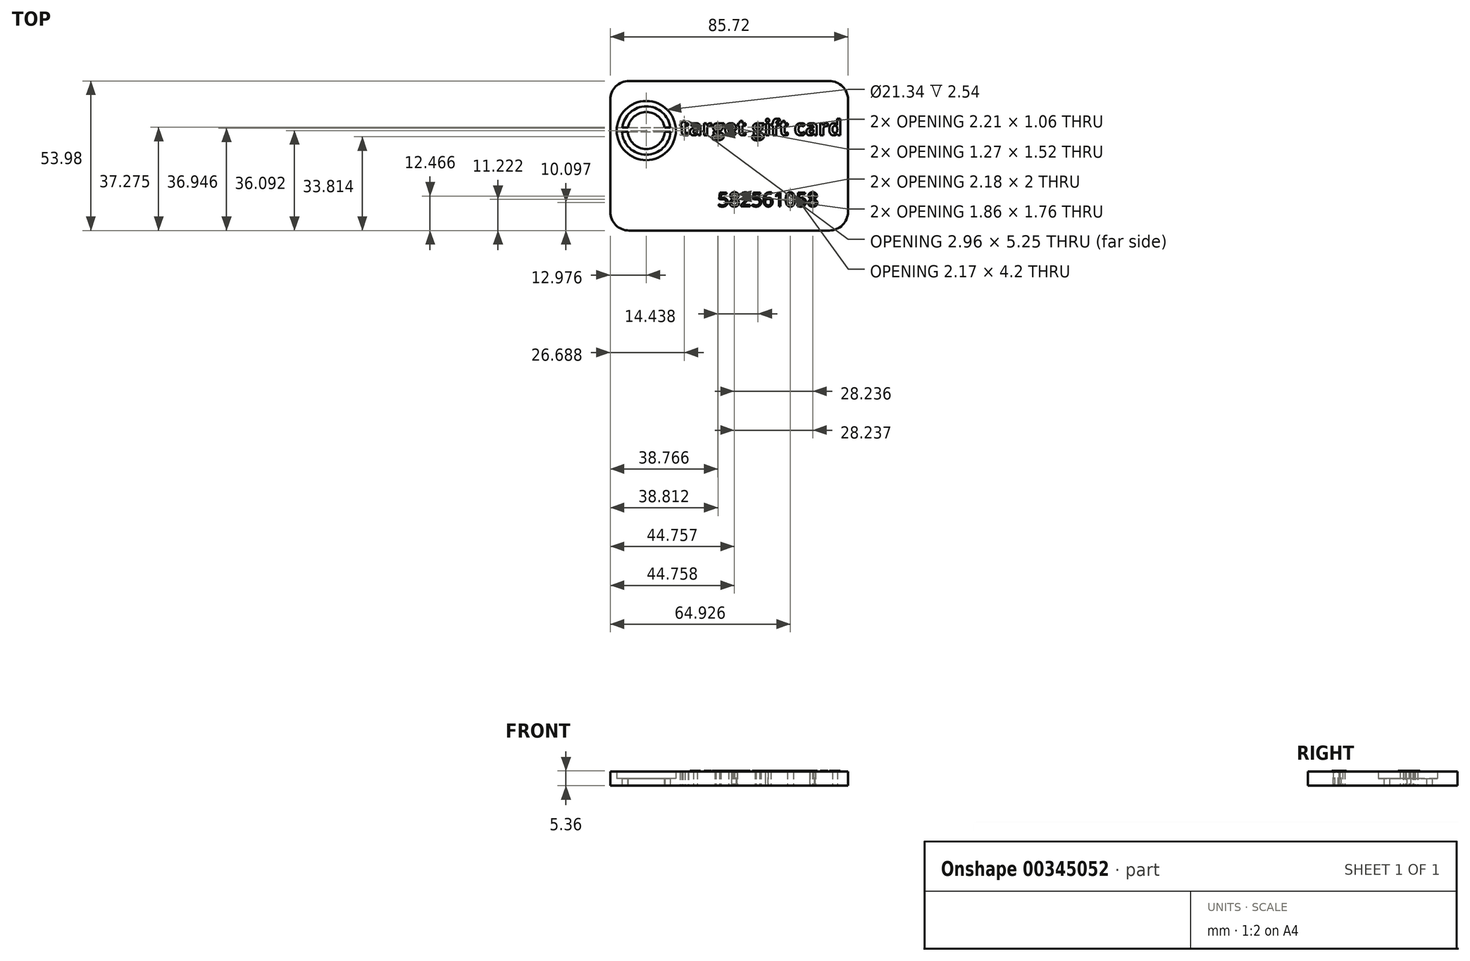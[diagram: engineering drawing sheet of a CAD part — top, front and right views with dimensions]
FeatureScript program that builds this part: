
annotation { "Feature Type Name" : "Feature", "Feature Type Description" : "" }
export const myFeature = defineFeature(function(context is Context, id is Id, definition is map)
    precondition{}
    {
        {
            var Q0;
            Q0=qCreatedBy(makeId("Top.planeOp"),FACE);
            var sketch = newSketch(context, id + "F0", { "sketchPlane" : qUnion([Q0])});
            skLineSegment(sketch, "E0.bottom", {"start": v(-45.51, 28) * mm, "end": v(40.21, 28) * mm});
            skLineSegment(sketch, "E0.top", {"start": v(-45.51, -25.97) * mm, "end": v(40.21, -25.97) * mm});
            skLineSegment(sketch, "E0.left", {"start": v(-45.51, 28) * mm, "end": v(-45.51, -25.97) * mm});
            skLineSegment(sketch, "E0.right", {"start": v(40.21, 28) * mm, "end": v(40.21, -25.97) * mm});
            skCircle(sketch, "E1", {"center": v(-32.53, 10.12) * mm, "radius": 6.68 * mm});
            skCircle(sketch, "E2", {"center": v(-32.53, 10.12) * mm, "radius": 8.74 * mm});
            skCircle(sketch, "E3", {"center": v(-32.53, 10.12) * mm, "radius": 10.67 * mm});
            skText(sketch, "E4", { "text": "target gift card", "fontName": "OpenSans-Bold.ttf"});
            skText(sketch, "E5", { "text": "582561058", "fontName": "OpenSans-Regular.ttf"});
            const initialGuessF0  = {"E4": [-0.02048, 0.00843, 1, 0, 0.00562], "E5": [-0.0068, -0.01727, 1, 0, 0.00508]};
            skSetInitialGuess(sketch, initialGuessF0);
            skSolve(sketch);
        }
        {
            var Q0;
            Q0=makeQuery(id+"F0.imprint","IMPRINT",FACE,{"disambiguationData":[TD([[makeQuery(id+"F0.imprint","IMPRINT",EDGE,{"derivedFrom":sQuery(id+"F0.wireOp",EDGE,"E1")}),1.0]])]});
            var Q1;
            Q1=makeQuery(id+"F0.imprint","IMPRINT",FACE,{"disambiguationData":[TD([[makeQuery(id+"F0.imprint","IMPRINT",EDGE,{"derivedFrom":sQuery(id+"F0.wireOp",EDGE,"E2")}),-1.0]])]});
            extrude(context, id + "F1", {"entities" : qUnion([Q0, Q1]), "depth" : 2.54 * mm});
        }
        {
            var Q0;
            Q0=makeQuery(id+"F0.imprint","IMPRINT",FACE,{"disambiguationData":[TD([[makeQuery(id+"F0.imprint","IMPRINT",EDGE,{"derivedFrom":sQuery(id+"F0.wireOp",EDGE,"E0.bottom")}),-1.0]])]});
            extrude(context, id + "F2", {"entities" : qUnion([Q0]), "operationType" : NewBodyOperationType.ADD, "depth" : 5.08 * mm});
        }
        {
            var Q0;
            Q0=makeQuery(id+"F0.imprint","IMPRINT",FACE,{"disambiguationData":[TD([[makeQuery(id+"F0.imprint","IMPRINT",EDGE,{"derivedFrom":sQuery(id+"F0.wireOp",EDGE,"E0.bottom")}),-1.0]])]});
            var sketch = newSketch(context, id + "F3", { "sketchPlane" : qUnion([Q0])});
            skLineSegment(sketch, "E6.bottom", {"start": v(-43.56, 9.69) * mm, "end": v(-22.85, 9.69) * mm});
            skLineSegment(sketch, "E6.top", {"start": v(-43.56, 11.26) * mm, "end": v(-22.85, 11.26) * mm});
            skLineSegment(sketch, "E6.left", {"start": v(-43.56, 9.69) * mm, "end": v(-43.56, 11.26) * mm});
            skLineSegment(sketch, "E6.right", {"start": v(-22.85, 9.69) * mm, "end": v(-22.85, 11.26) * mm});
            skSolve(sketch);
        }
        {
            var Q0;
            {var subQ0=sQuery(id+"F3.wireOp",EDGE,"E6.right");Q0=makeQuery(id+"F3.imprint","IMPRINT",FACE,{"disambiguationData":[TD([[makeQuery(id+"F3.imprint","IMPRINT",EDGE,{"derivedFrom":subQ0}),1.0]])]});}
            extrude(context, id + "F4", {"entities" : qUnion([Q0]), "operationType" : NewBodyOperationType.ADD, "endBound" : BoundingType.UP_TO_NEXT, "depth" : 25.4 * mm});
        }
        {
            var Q0;
            {var subQ0=sQuery(id+"F3.wireOp",EDGE,"E6.right");Q0=makeQuery(id+"F3.imprint","IMPRINT",FACE,{"disambiguationData":[TD([[makeQuery(id+"F3.imprint","IMPRINT",EDGE,{"derivedFrom":subQ0}),1.0]])]});}
            extrude(context, id + "F5", {"entities" : qUnion([Q0]), "operationType" : NewBodyOperationType.ADD, "depth" : 0 * mm});
        }
        {
            var Q0;
            {var subQ0=sQuery(id+"F3.wireOp",EDGE,"E6.right");Q0=makeQuery(id+"F3.imprint","IMPRINT",FACE,{"disambiguationData":[TD([[makeQuery(id+"F3.imprint","IMPRINT",EDGE,{"derivedFrom":subQ0}),1.0]])]});}
            extrude(context, id + "F6", {"entities" : qUnion([Q0]), "operationType" : NewBodyOperationType.ADD, "oppositeDirection" : true, "depth" : 0.03 * mm});
        }
        {
            var Q0;
            Q0=makeQuery(id+"F0.imprint","IMPRINT",FACE,{"disambiguationData":[TD([[makeQuery(id+"F0.imprint","IMPRINT",EDGE,{"derivedFrom":sQuery(id+"F0.wireOp",EDGE,"E4.sketch_text.stroke-209")}),-1.0]])]});
            var Q1;
            Q1=makeQuery(id+"F0.imprint","IMPRINT",FACE,{"disambiguationData":[TD([[makeQuery(id+"F0.imprint","IMPRINT",EDGE,{"derivedFrom":sQuery(id+"F0.wireOp",EDGE,"E4.sketch_text.stroke-191")}),-1.0]])]});
            var Q2;
            Q2=makeQuery(id+"F0.imprint","IMPRINT",FACE,{"disambiguationData":[TD([[makeQuery(id+"F0.imprint","IMPRINT",EDGE,{"derivedFrom":sQuery(id+"F0.wireOp",EDGE,"E4.sketch_text.stroke-187")}),-1.0]])]});
            var Q3;
            Q3=makeQuery(id+"F0.imprint","IMPRINT",FACE,{"disambiguationData":[TD([[makeQuery(id+"F0.imprint","IMPRINT",EDGE,{"derivedFrom":sQuery(id+"F0.wireOp",EDGE,"E4.sketch_text.stroke-182")}),-1.0]])]});
            var Q4;
            Q4=makeQuery(id+"F0.imprint","IMPRINT",FACE,{"disambiguationData":[TD([[makeQuery(id+"F0.imprint","IMPRINT",EDGE,{"derivedFrom":sQuery(id+"F0.wireOp",EDGE,"E4.sketch_text.stroke-138")}),-1.0]])]});
            var Q5;
            Q5=makeQuery(id+"F0.imprint","IMPRINT",FACE,{"disambiguationData":[TD([[makeQuery(id+"F0.imprint","IMPRINT",EDGE,{"derivedFrom":sQuery(id+"F0.wireOp",EDGE,"E4.sketch_text.stroke-120")}),-1.0]])]});
            var Q6;
            Q6=makeQuery(id+"F0.imprint","IMPRINT",FACE,{"disambiguationData":[TD([[makeQuery(id+"F0.imprint","IMPRINT",EDGE,{"derivedFrom":sQuery(id+"F0.wireOp",EDGE,"E4.sketch_text.stroke-100")}),-1.0]])]});
            var Q7;
            Q7=makeQuery(id+"F0.imprint","IMPRINT",FACE,{"disambiguationData":[TD([[makeQuery(id+"F0.imprint","IMPRINT",EDGE,{"derivedFrom":sQuery(id+"F0.wireOp",EDGE,"E4.sketch_text.stroke-56")}),-1.0]])]});
            var Q8;
            Q8=makeQuery(id+"F0.imprint","IMPRINT",FACE,{"disambiguationData":[TD([[makeQuery(id+"F0.imprint","IMPRINT",EDGE,{"derivedFrom":sQuery(id+"F0.wireOp",EDGE,"E4.sketch_text.stroke-43")}),-1.0]])]});
            var Q9;
            Q9=makeQuery(id+"F0.imprint","IMPRINT",FACE,{"disambiguationData":[TD([[makeQuery(id+"F0.imprint","IMPRINT",EDGE,{"derivedFrom":sQuery(id+"F0.wireOp",EDGE,"E4.sketch_text.stroke-18")}),-1.0]])]});
            var Q10;
            Q10=makeQuery(id+"F0.imprint","IMPRINT",FACE,{"disambiguationData":[TD([[makeQuery(id+"F0.imprint","IMPRINT",EDGE,{"derivedFrom":sQuery(id+"F0.wireOp",EDGE,"E4.sketch_text.stroke-227")}),-1.0]])]});
            var Q11;
            Q11=makeQuery(id+"F0.imprint","IMPRINT",FACE,{"disambiguationData":[TD([[makeQuery(id+"F0.imprint","IMPRINT",EDGE,{"derivedFrom":sQuery(id+"F0.wireOp",EDGE,"E4.sketch_text.stroke-241")}),-1.0]])]});
            var Q12;
            Q12=makeQuery(id+"F0.imprint","IMPRINT",FACE,{"disambiguationData":[TD([[makeQuery(id+"F0.imprint","IMPRINT",EDGE,{"derivedFrom":sQuery(id+"F0.wireOp",EDGE,"E4.sketch_text.stroke-266")}),-1.0]])]});
            var Q13;
            Q13=makeQuery(id+"F0.imprint","IMPRINT",FACE,{"disambiguationData":[TD([[makeQuery(id+"F0.imprint","IMPRINT",EDGE,{"derivedFrom":sQuery(id+"F0.wireOp",EDGE,"E4.sketch_text.stroke-279")}),-1.0]])]});
            var Q14;
            Q14=makeQuery(id+"F0.imprint","IMPRINT",FACE,{"disambiguationData":[TD([[makeQuery(id+"F0.imprint","IMPRINT",EDGE,{"derivedFrom":sQuery(id+"F0.wireOp",EDGE,"E5.sketch_text.stroke-0")}),-1.0]])]});
            var Q15;
            Q15=makeQuery(id+"F0.imprint","IMPRINT",FACE,{"disambiguationData":[TD([[makeQuery(id+"F0.imprint","IMPRINT",EDGE,{"derivedFrom":sQuery(id+"F0.wireOp",EDGE,"E5.sketch_text.stroke-19")}),-1.0]])]});
            var Q16;
            Q16=makeQuery(id+"F0.imprint","IMPRINT",FACE,{"disambiguationData":[TD([[makeQuery(id+"F0.imprint","IMPRINT",EDGE,{"derivedFrom":sQuery(id+"F0.wireOp",EDGE,"E5.sketch_text.stroke-114")}),-1.0]])]});
            var Q17;
            Q17=makeQuery(id+"F0.imprint","IMPRINT",FACE,{"disambiguationData":[TD([[makeQuery(id+"F0.imprint","IMPRINT",EDGE,{"derivedFrom":sQuery(id+"F0.wireOp",EDGE,"E5.sketch_text.stroke-89")}),-1.0]])]});
            var Q18;
            Q18=makeQuery(id+"F0.imprint","IMPRINT",FACE,{"disambiguationData":[TD([[makeQuery(id+"F0.imprint","IMPRINT",EDGE,{"derivedFrom":sQuery(id+"F0.wireOp",EDGE,"E5.sketch_text.stroke-70")}),-1.0]])]});
            var Q19;
            Q19=makeQuery(id+"F0.imprint","IMPRINT",FACE,{"disambiguationData":[TD([[makeQuery(id+"F0.imprint","IMPRINT",EDGE,{"derivedFrom":sQuery(id+"F0.wireOp",EDGE,"E5.sketch_text.stroke-50")}),-1.0]])]});
            var Q20;
            Q20=makeQuery(id+"F0.imprint","IMPRINT",FACE,{"disambiguationData":[TD([[makeQuery(id+"F0.imprint","IMPRINT",EDGE,{"derivedFrom":sQuery(id+"F0.wireOp",EDGE,"E5.sketch_text.stroke-123")}),-1.0]])]});
            var Q21;
            Q21=makeQuery(id+"F0.imprint","IMPRINT",FACE,{"disambiguationData":[TD([[makeQuery(id+"F0.imprint","IMPRINT",EDGE,{"derivedFrom":sQuery(id+"F0.wireOp",EDGE,"E5.sketch_text.stroke-139")}),-1.0]])]});
            var Q22;
            Q22=makeQuery(id+"F0.imprint","IMPRINT",FACE,{"disambiguationData":[TD([[makeQuery(id+"F0.imprint","IMPRINT",EDGE,{"derivedFrom":sQuery(id+"F0.wireOp",EDGE,"E5.sketch_text.stroke-158")}),-1.0]])]});
            extrude(context, id + "F7", {"entities" : qUnion([Q0, Q1, Q2, Q3, Q4, Q5, Q6, Q7, Q8, Q9, Q10, Q11, Q12, Q13, Q14, Q15, Q16, Q17, Q18, Q19, Q20, Q21, Q22]), "operationType" : NewBodyOperationType.ADD, "depth" : 5.33 * mm});
        }
        {
            var Q0;
            Q0=makeQuery(id+"F2.opExtrude","SWEPT_EDGE",EDGE,{"disambiguationData":[OSD([sQuery(id+"F0.wireOp",EDGE,"E0.top"),sQuery(id+"F0.wireOp",EDGE,"E0.right")])]});
            var Q1;
            Q1=makeQuery(id+"F2.opExtrude","SWEPT_EDGE",EDGE,{"disambiguationData":[OSD([sQuery(id+"F0.wireOp",EDGE,"E0.bottom"),sQuery(id+"F0.wireOp",EDGE,"E0.right")])]});
            var Q2;
            Q2=makeQuery(id+"F2.opExtrude","SWEPT_EDGE",EDGE,{"disambiguationData":[OSD([sQuery(id+"F0.wireOp",EDGE,"E0.bottom"),sQuery(id+"F0.wireOp",EDGE,"E0.left")])]});
            var Q3;
            Q3=makeQuery(id+"F2.opExtrude","SWEPT_EDGE",EDGE,{"disambiguationData":[OSD([sQuery(id+"F0.wireOp",EDGE,"E0.top"),sQuery(id+"F0.wireOp",EDGE,"E0.left")])]});
            fillet(context, id + "F8", {"entities" : qUnion([Q0, Q1, Q2, Q3]), "radius" : 6.75 * mm, "tangentPropagation" : true, "allowEdgeOverflow" : false});
        }
        {
            var Q0;
            Q0=makeQuery(id+"F5.boolean.opBoolean","SPLIT",FACE,{"disambiguationData":[OD(1.0)],"derivedFrom":makeQuery(id+"F5.opExtrude","CAP_FACE",FACE,{"disambiguationData":[OSD([sQuery(id+"F0.wireOp",EDGE,"E3"),sQuery(id+"F3.wireOp",EDGE,"E6.bottom"),sQuery(id+"F3.wireOp",EDGE,"E6.top"),sQuery(id+"F3.wireOp",EDGE,"E6.right")])],"isStart":false})});
            var Q1;
            Q1=makeQuery(id+"F5.boolean.opBoolean","SPLIT",FACE,{"disambiguationData":[OD(0.0)],"derivedFrom":makeQuery(id+"F5.opExtrude","CAP_FACE",FACE,{"disambiguationData":[OSD([sQuery(id+"F0.wireOp",EDGE,"E3"),sQuery(id+"F3.wireOp",EDGE,"E6.bottom"),sQuery(id+"F3.wireOp",EDGE,"E6.top"),sQuery(id+"F3.wireOp",EDGE,"E6.right")])],"isStart":false})});
            var Q2;
            Q2=makeQuery(id+"F1.opExtrude","CAP_FACE",FACE,{"disambiguationData":[OSD([sQuery(id+"F0.wireOp",EDGE,"E1")])],"isStart":false});
            extrude(context, id + "F9", {"entities" : qUnion([Q0, Q1]), "operationType" : NewBodyOperationType.ADD, "endBound" : BoundingType.UP_TO_SURFACE, "endBoundEntityFace" : qUnion([Q2]), "depth" : 25.4 * mm});
        }
    });
